# Revit family: TV-297_RFA
name_source: partatom
category: Aparatos sanitarios
units: mm (PartAtom-declared; Revit-internal decimal feet)

## family parameters
Compartido = Sí
Corte con vacíos al cargar = No
Cota de conector redondo = Diámetro de uso
Número OmniClass = 23.45.00.00
Punto de cálculo de habitación = Sí
Se basa en plano de trabajo = Sí
Siempre vertical = Sí
Tipo de pieza = Normal
Título OmniClass = Sanitary, Laundry, and Cleaning Equipment

## types (1)
- TV-297_RFA
    Batterías = 6 baterías alcalinas AA
    Chrome = Brass Chromed
    Comentarios de tipo = Línea Electronica
    Conexión AF = Sí
    Connection = ½" - 14 NPSM
    Descripción = Llave de Lavabo Electrónica de Sensor de Baterías
    Detection Range = Distancia de detección 12 cm (ajuste de fibrica)
    Elevación por Defecto = 1"
    Elevación por defecto = 48"
    Fabricante = Helvex
    Imagen de tipo = <Ninguno>
    Max. Working Pressure = 85.3 psi
    Min. Working Pressure = 5.7 psi
    Modelo = TV-297
    Operación = Active la salida colocando su mano dentro de la zona de detección.
    Potencia = 3 W
    Tensión de alimentación = 9 V
    Total Height = 7"
    Total Lenght = 7"
    Total Width = 2"
    URL = http://172.16.0.178

## geometry (parser evidence)
native form markers: Sweep x3
no freeform markers — native parametric forms only
